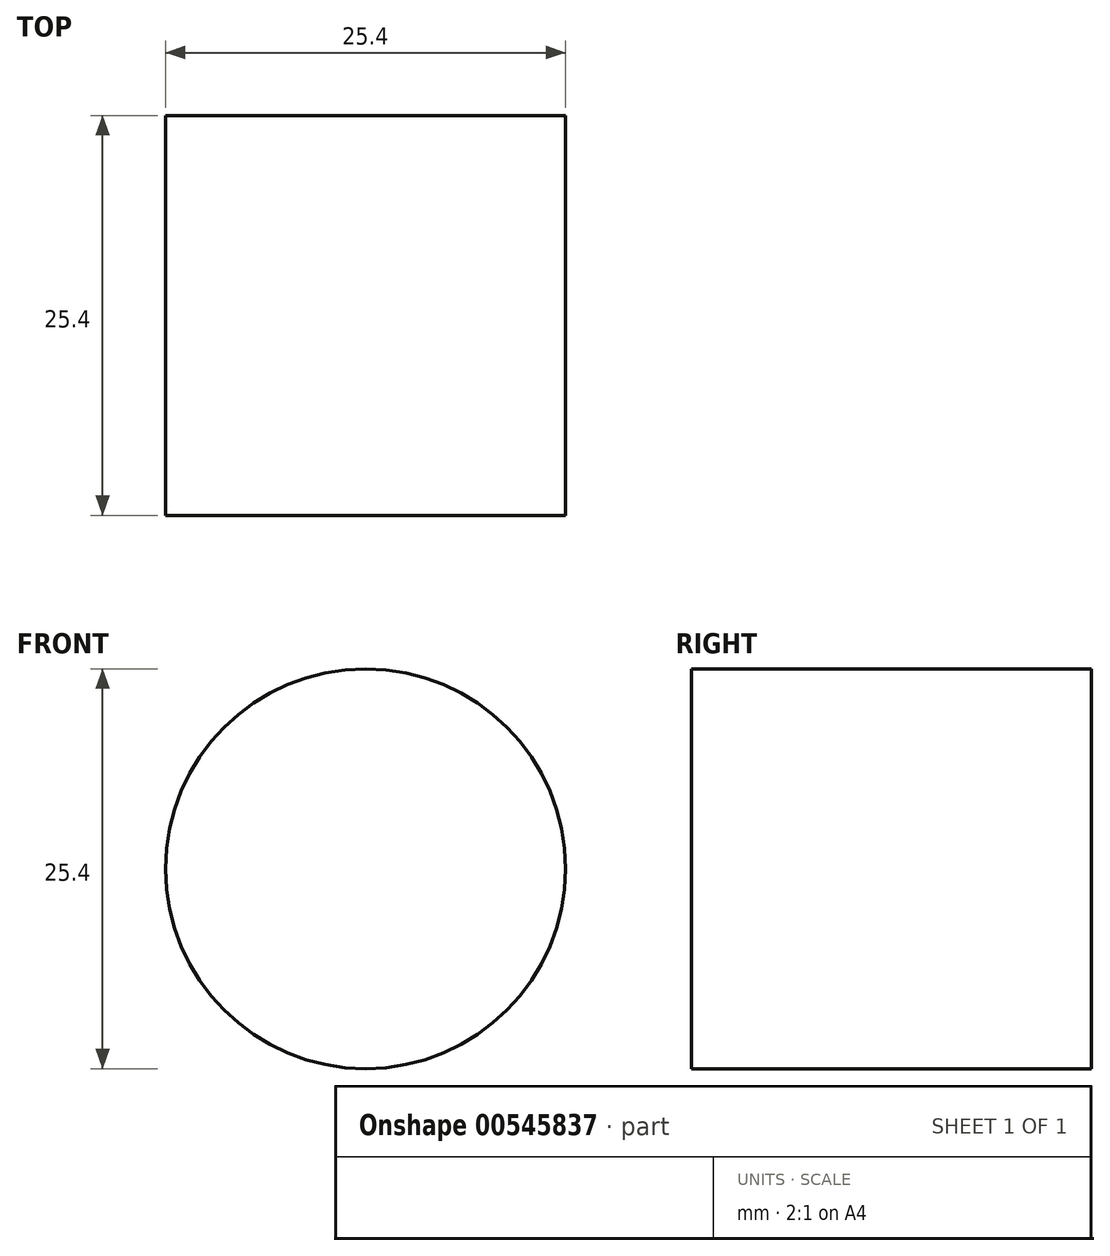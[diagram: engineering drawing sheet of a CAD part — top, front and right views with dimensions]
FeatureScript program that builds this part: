
annotation { "Feature Type Name" : "Feature", "Feature Type Description" : "" }
export const myFeature = defineFeature(function(context is Context, id is Id, definition is map)
    precondition{}
    {
        {
            var Q0;
            Q0=qCreatedBy(makeId("Front.planeOp"),FACE);
            var sketch = newSketch(context, id + "F0", { "sketchPlane" : qUnion([Q0])});
            skCircle(sketch, "E0", {"center": v(0, 0) * mm, "radius": 12.7 * mm});
            skSolve(sketch);
        }
        {
            var Q0;
            Q0=sQuery(id+"F0.wireOp",EDGE,"E0");
            extrude(context, id + "F1", {"bodyType" : ToolBodyType.SURFACE, "surfaceEntities" : qUnion([Q0]), "depth" : 25.4 * mm, "offsetDistance" : 25.4 * mm});
        }
    });
